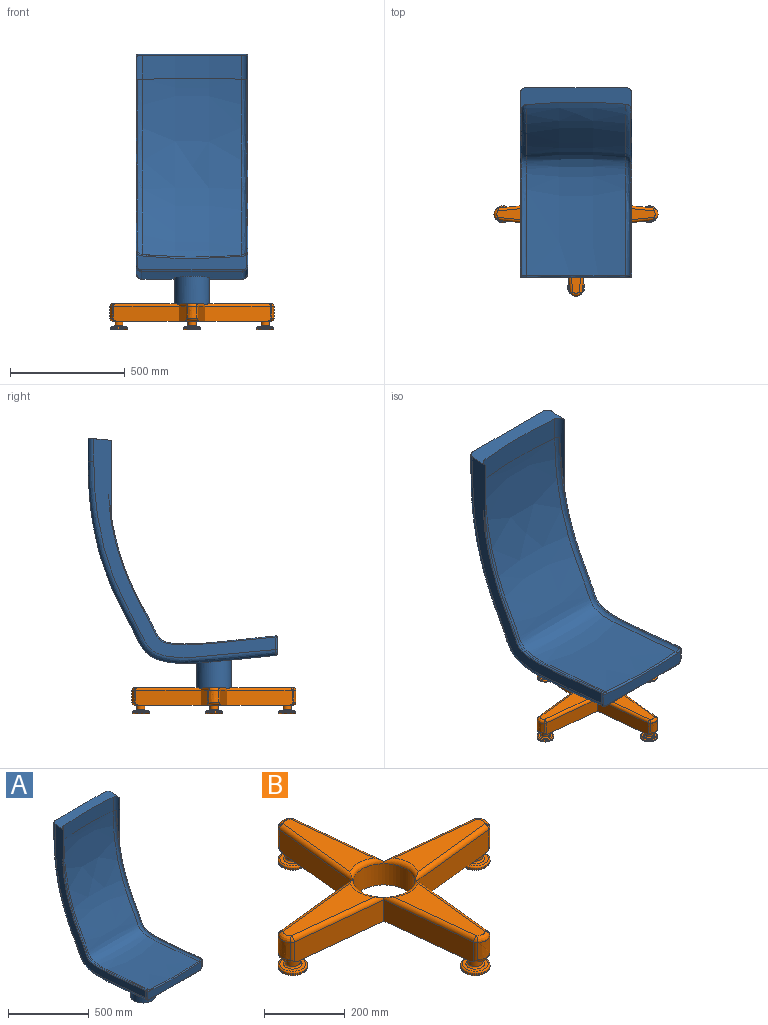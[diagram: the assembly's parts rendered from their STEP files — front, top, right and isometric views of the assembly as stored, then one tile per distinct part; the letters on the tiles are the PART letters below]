
ASSEMBLY  parts=2 mates=1
PART A: 32 faces, bbox 542.8x829.8x1166.2 mm
  f0: plane 475.5x70.44mm, normal (0,-1,0), area 25588.9mm2, adj f20,f21,f24,f27,f28,f29,f30,f31
  f1: plane 488.49x102.02mm, normal (0,-0.09,1), area 32428.5mm2, adj f5,f9,f10,f11,f12,f13,f14,f15
  f2: bspline ~799.51x751.51mm, area 30451.7mm2, adj f3,f10,f19,f24
  f3: bspline ~815.71x766.38mm, area 585202.1mm2, adj f2,f4,f11,f20
  f4: bspline ~801.59x753.41mm, area 30124.7mm2, adj f3,f12,f18,f21
  f5: plane 957.54x799.09mm, normal (1,0,0), area 80510.1mm2, adj f1,f6,f12,f13,f18,f22,f27
  f6: bspline ~879.01x824.51mm, area 57616.4mm2, adj f5,f7,f13,f29
  f7: bspline ~879.01x824.51mm, area 620469.1mm2, adj f6,f8,f14,f16,f31
  f8: bspline ~879.01x824.51mm, area 57616.2mm2, adj f7,f9,f15,f30
  f9: plane 956.91x797.01mm, normal (-1,0,0), area 80886mm2, adj f1,f8,f10,f15,f19,f23,f28
  f10: bspline ~359.66x28.24mm, area 6910mm2, adj f1,f2,f9,f11,f19
  f11: bspline ~432.08x102.57mm, area 43964.8mm2, adj f1,f3,f10,f12
  f12: bspline ~374.16x30.14mm, area 7486.5mm2, adj f1,f4,f5,f11,f18
  f13: bspline ~103.83x25.4mm, area 4045.9mm2, adj f1,f5,f6,f14
  f14: plane 436.88x101.6mm, normal (0,1,0), area 44387mm2, adj f1,f7,f13,f15
  f15: bspline ~103.83x25.4mm, area 4045.9mm2, adj f1,f8,f9,f14
  f16: cylinder r=76.2mm len=188.69mm, axis (0,0,1), area 90338.5mm2, adj f7,f17
  f17: plane 152.4x152.4mm, normal (0,0,-1), area 18241.5mm2, adj f16
  f18: bspline ~797.13x745.63mm, area 13070.5mm2, adj f4,f5,f12,f22
  f19: bspline ~796.87x744.66mm, area 13114.5mm2, adj f2,f9,f10,f23
  f20: bspline ~531.4x25.74mm, area 4384.6mm2, adj f0,f3,f21,f24
  f21: bspline ~29.34x17.46mm, area 229.9mm2, adj f0,f4,f20,f22,f25
  f22: bspline ~11.82x7.96mm, area 4.3mm2, adj f5,f18,f21,f25
  f23: bspline ~11.87x7.97mm, area 4.3mm2, adj f9,f19,f24,f26
  f24: bspline ~26.64x17.58mm, area 232.7mm2, adj f0,f2,f20,f23,f26
  f25: bspline ~15.45x11.05mm, area 59.7mm2, adj f21,f22,f27
  f26: bspline ~15.52x8.48mm, area 60.1mm2, adj f23,f24,f28
  f27: cylinder r=6.1mm len=52.65mm, axis (0,0,-1), area 486.7mm2, adj f0,f5,f25,f29
  f28: cylinder r=6.1mm len=54.82mm, axis (0,0,-1), area 507.4mm2, adj f0,f9,f26,f30
  f29: bspline ~31.76x25.55mm, area 334.4mm2, adj f0,f6,f27,f31
  f30: bspline ~31.77x25.55mm, area 334.4mm2, adj f0,f8,f28,f31
  f31: cylinder r=6.1mm len=436.88mm, axis (-1,0,0), area 3940mm2, adj f0,f7,f29,f30
PART B: 79 faces, bbox 717.9x717.9x114.4 mm
  f0: plane 266.84x82.52mm, normal (0,0,1), area 13947.6mm2, adj f51,f65,f66,f71
  f1: plane 266.84x82.52mm, normal (0,0,1), area 13947.6mm2, adj f54,f67,f68,f71
  f2: plane 266.84x82.52mm, normal (0,0,1), area 13947.6mm2, adj f69,f71,f73,f74
  f3: plane 284.79x64.57mm, normal (0.1,0.99,0), area 18273.4mm2, adj f4,f17,f48,f56,f70
  f4: plane 284.78x64.56mm, normal (0.99,0.1,0), area 18273.4mm2, adj f3,f17,f73,f77,f78
  f5: extruded ~51.82x43.54mm, area 2491.7mm2, adj f74,f75,f77,f78
  f6: plane 284.79x64.57mm, normal (-0.99,0.1,0), area 18273.4mm2, adj f7,f17,f69,f75,f77
  f7: plane 284.78x64.56mm, normal (-0.1,0.99,0), area 18273.4mm2, adj f6,f17,f47,f55,f68
  f8: extruded ~51.82x43.54mm, area 2491.7mm2, adj f47,f53,f54,f55
  f9: plane 284.79x64.57mm, normal (-0.1,-0.99,0), area 18273.4mm2, adj f10,f17,f47,f53,f67
  f10: plane 284.78x64.56mm, normal (-0.99,-0.1,0), area 18273.4mm2, adj f9,f17,f46,f52,f66
  f11: extruded ~51.82x43.54mm, area 2491.7mm2, adj f46,f50,f51,f52
  f12: plane 284.79x64.57mm, normal (0.99,-0.1,0), area 18273.4mm2, adj f13,f17,f46,f50,f65
  f13: plane 284.78x64.56mm, normal (0.1,-0.99,0), area 18273.4mm2, adj f12,f17,f48,f49,f64
  f14: extruded ~51.82x43.54mm, area 2491.7mm2, adj f48,f49,f56,f57
  f15: cylinder r=76.2mm len=152.4mm, axis (0,0,-1), area 30645.7mm2, adj f17,f71
  f16: plane 266.84x82.52mm, normal (0,0,1), area 13947.9mm2, adj f57,f64,f70,f71
  f17: plane 690.03x690.03mm, normal (0,0,-1), area 82797.3mm2, adj f3,f4,f6,f7,f9,f10,f12,f13
  f18: cylinder r=18.29mm len=36.58mm, axis (0,0,1), area 2393.3mm2, adj f17,f45
  f19: cylinder r=18.29mm len=36.58mm, axis (0,0,1), area 2393.3mm2, adj f17,f44
  f20: cylinder r=18.29mm len=36.58mm, axis (0,0,1), area 2393.3mm2, adj f17,f43
  f21: cylinder r=18.29mm len=36.58mm, axis (0,0,1), area 2393.3mm2, adj f17,f42
  f22: cylinder r=36.58mm len=73.15mm, axis (0,0,1), area 700.5mm2, adj f34,f35
  f23: plane 64.01x64.01mm, normal (0,0,-1), area 3217.8mm2, adj f35
  f24: plane 64.01x64.01mm, normal (0,0,1), area 1576.1mm2, adj f34,f45
  f25: cylinder r=36.58mm len=73.15mm, axis (0,0,1), area 700.5mm2, adj f40,f41
  f26: plane 64.01x64.01mm, normal (0,0,-1), area 3217.8mm2, adj f41
  f27: plane 64.01x64.01mm, normal (0,0,1), area 1576.1mm2, adj f40,f44
  f28: cylinder r=36.58mm len=73.15mm, axis (0,0,1), area 700.5mm2, adj f38,f39
  f29: plane 64.01x64.01mm, normal (0,0,-1), area 3217.8mm2, adj f39
  f30: plane 64.01x64.01mm, normal (0,0,1), area 1576.1mm2, adj f38,f43
  f31: cylinder r=36.58mm len=73.15mm, axis (0,0,1), area 700.5mm2, adj f36,f37
  f32: plane 64.01x64.01mm, normal (0,0,-1), area 3217.8mm2, adj f37
  f33: plane 64.01x64.01mm, normal (0,0,1), area 1576.1mm2, adj f36,f42
  f34: torus R=32mm, axis (0,0,-1), area 1575.5mm2, adj f22,f24
  f35: torus R=32mm, axis (0,0,-1), area 1575.5mm2, adj f22,f23
  f36: torus R=32mm, axis (0,0,-1), area 1575.5mm2, adj f31,f33
  f37: torus R=32mm, axis (0,0,-1), area 1575.5mm2, adj f31,f32
  f38: torus R=32mm, axis (0,0,-1), area 1575.5mm2, adj f28,f30
  f39: torus R=32mm, axis (0,0,-1), area 1575.5mm2, adj f28,f29
  f40: torus R=32mm, axis (0,0,-1), area 1575.5mm2, adj f25,f27
  f41: torus R=32mm, axis (0,0,-1), area 1575.5mm2, adj f25,f26
  f42: torus R=22.86mm, axis (0,0,-1), area 900.2mm2, adj f21,f33
  f43: torus R=22.86mm, axis (0,0,-1), area 900.2mm2, adj f20,f30
  f44: torus R=22.86mm, axis (0,0,-1), area 900.2mm2, adj f19,f27
  f45: torus R=22.86mm, axis (0,0,-1), area 900.2mm2, adj f18,f24
  f46: bspline ~111.61x65.19mm, area 1168.7mm2, adj f10,f11,f12,f17,f50,f52
  f47: bspline ~111.61x65.19mm, area 1168.7mm2, adj f7,f8,f9,f17,f53,f55
  f48: bspline ~111.61x65.19mm, area 1168.7mm2, adj f3,f13,f14,f17,f49,f56
  f49: cylinder r=12.19mm len=59.81mm, axis (0,0,-1), area 527.8mm2, adj f13,f14,f48,f58
  f50: cylinder r=12.19mm len=59.81mm, axis (0,0,-1), area 527.8mm2, adj f11,f12,f46,f59
  f51: bspline ~46.22x19.53mm, area 803.7mm2, adj f0,f11,f59,f60
  f52: cylinder r=12.19mm len=59.81mm, axis (0,0,-1), area 527.8mm2, adj f10,f11,f46,f60
  f53: cylinder r=12.19mm len=59.81mm, axis (0,0,-1), area 527.8mm2, adj f8,f9,f47,f61
  f54: bspline ~46.22x19.53mm, area 803.7mm2, adj f1,f8,f61,f62
  f55: cylinder r=12.19mm len=59.81mm, axis (0,0,-1), area 527.8mm2, adj f7,f8,f47,f62
  f56: cylinder r=12.19mm len=59.81mm, axis (0,0,-1), area 527.8mm2, adj f3,f14,f48,f63
  f57: bspline ~46.22x19.53mm, area 803.7mm2, adj f14,f16,f58,f63
  f58: sphere r=12.19mm, area 73.4mm2, adj f49,f57,f64
  f59: sphere r=12.19mm, area 115.3mm2, adj f50,f51,f65
  f60: sphere r=12.19mm, area 120.9mm2, adj f51,f52,f66
  f61: sphere r=12.19mm, area 115.3mm2, adj f53,f54,f67
  f62: sphere r=12.19mm, area 120.9mm2, adj f54,f55,f68
  f63: sphere r=12.19mm, area 152.6mm2, adj f56,f57,f70
  f64: cylinder r=12.19mm len=286.48mm, axis (-0.99,-0.1,0), area 5320.5mm2, adj f13,f16,f58,f65,f71
  f65: cylinder r=12.19mm len=286.48mm, axis (-0.1,-0.99,0), area 5320.5mm2, adj f0,f12,f59,f64,f71
  f66: cylinder r=12.19mm len=286.48mm, axis (-0.1,0.99,0), area 5320.5mm2, adj f0,f10,f60,f67,f71
  f67: cylinder r=12.19mm len=286.48mm, axis (-0.99,0.1,0), area 5320.5mm2, adj f1,f9,f61,f66,f71
  f68: cylinder r=12.19mm len=286.48mm, axis (0.99,0.1,0), area 5320.5mm2, adj f1,f7,f62,f69,f71
  f69: cylinder r=12.19mm len=286.48mm, axis (0.1,0.99,0), area 5320.5mm2, adj f2,f6,f68,f71,f72
  f70: cylinder r=12.19mm len=286.48mm, axis (0.99,-0.1,0), area 5320.5mm2, adj f3,f16,f63,f71,f73
  f71: torus R=88.39mm, axis (0,0,1), area 8325.3mm2, adj f0,f1,f2,f15,f16,f64,f65,f66
  f72: sphere r=12.19mm, area 67.8mm2, adj f69,f74,f75
  f73: cylinder r=12.19mm len=286.48mm, axis (0.1,-0.99,0), area 5320.5mm2, adj f2,f4,f70,f71,f76
  f74: bspline ~46.22x19.53mm, area 803.7mm2, adj f2,f5,f72,f76
  f75: cylinder r=12.19mm len=59.81mm, axis (0,0,-1), area 527.8mm2, adj f5,f6,f72,f77
  f76: sphere r=12.19mm, area 120.9mm2, adj f73,f74,f78
  f77: bspline ~111.61x65.19mm, area 1168.7mm2, adj f4,f5,f6,f17,f75,f78
  f78: cylinder r=12.19mm len=59.81mm, axis (0,0,-1), area 527.8mm2, adj f4,f5,f76,f77
PLACE A t=(-218.72,-275.97,291.71)mm
PLACE B t=(-218.72,0,-0.39)mm
MATE fastened A.f16 <-> B.f15  axis (0,0,-1) through (-218.72,0,-0.39)mm
